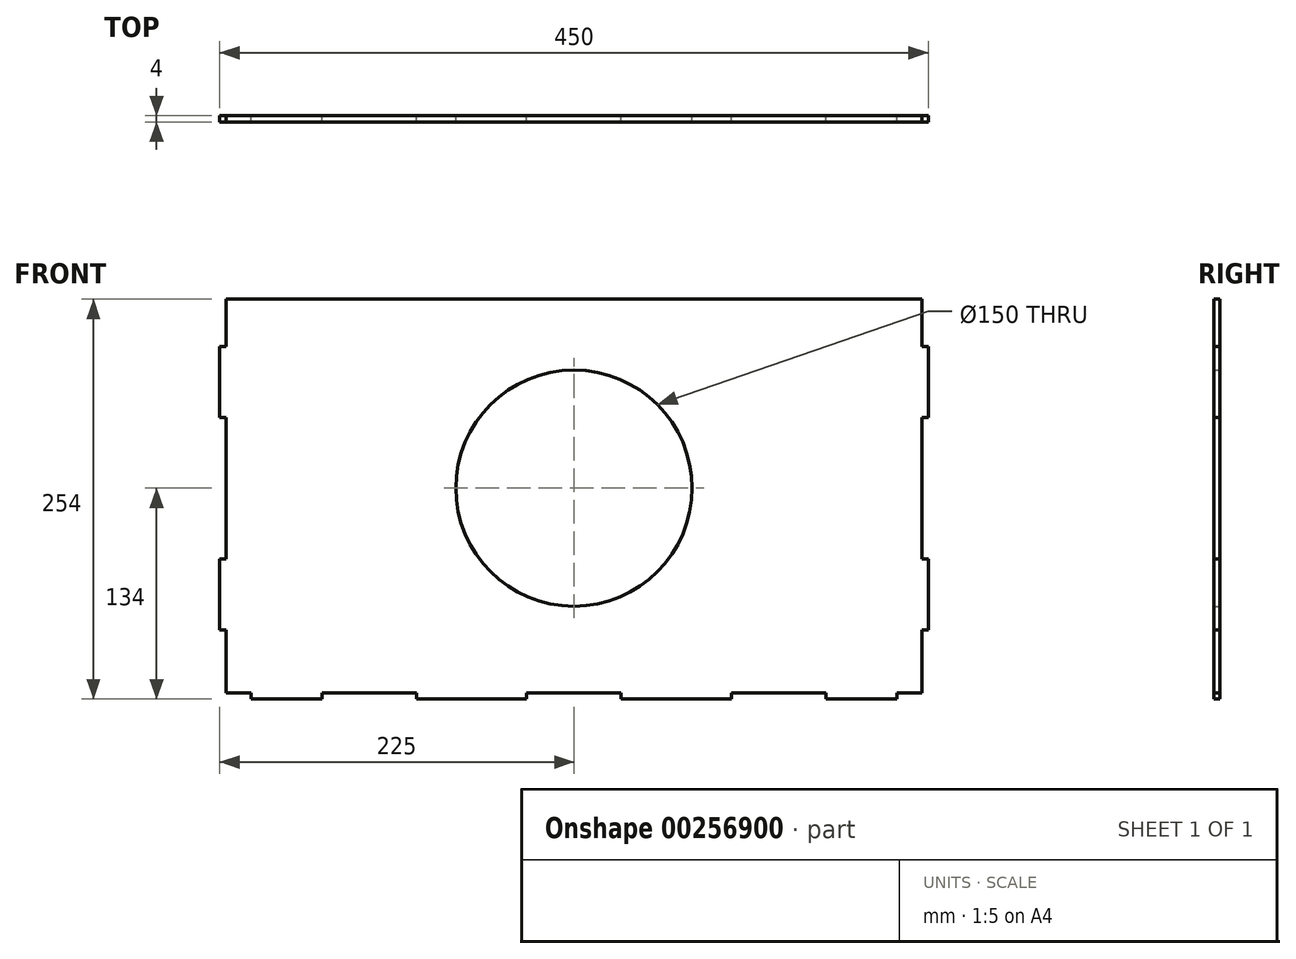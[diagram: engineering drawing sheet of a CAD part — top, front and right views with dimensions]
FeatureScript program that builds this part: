
annotation { "Feature Type Name" : "Feature", "Feature Type Description" : "" }
export const myFeature = defineFeature(function(context is Context, id is Id, definition is map)
    precondition{}
    {
        {
            var Q0;
            Q0=qCreatedBy(makeId("Front.planeOp"),FACE);
            var sketch = newSketch(context, id + "F0", { "sketchPlane" : qUnion([Q0])});
            skLineSegment(sketch, "E0.bottom", {"start": v(-4, 0) * mm, "end": v(-20, 0) * mm});
            skLineSegment(sketch, "E0.top", {"start": v(-4, 250) * mm, "end": v(-446, 250) * mm});
            skLineSegment(sketch, "E0.left", {"start": v(0, 40) * mm, "end": v(0, 85) * mm});
            skLineSegment(sketch, "E1.left", {"start": v(-20, 0) * mm, "end": v(-20, 0) * mm});
            skLineSegment(sketch, "E2", {"start": v(-65, 0) * mm, "end": v(-125, 0) * mm});
            skLineSegment(sketch, "E3", {"start": v(-325, 0) * mm, "end": v(-385, 0) * mm});
            skLineSegment(sketch, "E4", {"start": v(-430, 0) * mm, "end": v(-446, 0) * mm});
            skLineSegment(sketch, "E5", {"start": v(-195, 0) * mm, "end": v(-255, 0) * mm});
            skLineSegment(sketch, "E6", {"start": v(-20, 0) * mm, "end": v(-20, -4) * mm});
            skLineSegment(sketch, "E7", {"start": v(-20, -4) * mm, "end": v(-65, -4) * mm});
            skLineSegment(sketch, "E8", {"start": v(-65, -4) * mm, "end": v(-65, 0) * mm});
            skLineSegment(sketch, "E9", {"start": v(-125, 0) * mm, "end": v(-125, -4) * mm});
            skLineSegment(sketch, "E10", {"start": v(-125, -4) * mm, "end": v(-195, -4) * mm});
            skLineSegment(sketch, "E11", {"start": v(-195, -4) * mm, "end": v(-195, 0) * mm});
            skLineSegment(sketch, "E12", {"start": v(-255, 0) * mm, "end": v(-255, -4) * mm});
            skLineSegment(sketch, "E13", {"start": v(-255, -4) * mm, "end": v(-325, -4) * mm});
            skLineSegment(sketch, "E14", {"start": v(-325, -4) * mm, "end": v(-325, 0) * mm});
            skLineSegment(sketch, "E15", {"start": v(-385, -4) * mm, "end": v(-430, -4) * mm});
            skLineSegment(sketch, "E16", {"start": v(-430, -4) * mm, "end": v(-430, 0) * mm});
            skLineSegment(sketch, "E17", {"start": v(-385, -4) * mm, "end": v(-385, 0) * mm});
            skLineSegment(sketch, "E18.top", {"start": v(-450, 220) * mm, "end": v(-446, 220) * mm});
            skLineSegment(sketch, "E18.right", {"start": v(-446, 250) * mm, "end": v(-446, 220) * mm});
            skLineSegment(sketch, "E19.bottom", {"start": v(-450, 175) * mm, "end": v(-446, 175) * mm});
            skLineSegment(sketch, "E19.top", {"start": v(-450, 85) * mm, "end": v(-446, 85) * mm});
            skLineSegment(sketch, "E19.right", {"start": v(-446, 175) * mm, "end": v(-446, 85) * mm});
            skLineSegment(sketch, "E20.bottom", {"start": v(-450, 40) * mm, "end": v(-446, 40) * mm});
            skLineSegment(sketch, "E20.right", {"start": v(-446, 40) * mm, "end": v(-446, 0) * mm});
            skLineSegment(sketch, "E21", {"start": v(-450, 40) * mm, "end": v(-450, 85) * mm});
            skLineSegment(sketch, "E22", {"start": v(-450, 175) * mm, "end": v(-450, 220) * mm});
            skLineSegment(sketch, "E23", {"start": v(-4, 0) * mm, "end": v(-4, 40) * mm});
            skLineSegment(sketch, "E24", {"start": v(-4, 40) * mm, "end": v(0, 40) * mm});
            skLineSegment(sketch, "E25", {"start": v(0, 85) * mm, "end": v(-4, 85) * mm});
            skLineSegment(sketch, "E26", {"start": v(-4, 85) * mm, "end": v(-4, 175) * mm});
            skLineSegment(sketch, "E27", {"start": v(-4, 175) * mm, "end": v(0, 175) * mm});
            skLineSegment(sketch, "E28", {"start": v(0, 220) * mm, "end": v(-4, 220) * mm});
            skLineSegment(sketch, "E29", {"start": v(0, 175) * mm, "end": v(0, 220) * mm});
            skLineSegment(sketch, "E30", {"start": v(-4, 220) * mm, "end": v(-4, 250) * mm});
            skSolve(sketch);
        }
        {
            var Q0;
            Q0=makeQuery(id+"F0.imprint","IMPRINT",FACE,{"disambiguationData":[TD([[makeQuery(id+"F0.imprint","IMPRINT",EDGE,{"derivedFrom":sQuery(id+"F0.wireOp",EDGE,"E0.bottom")}),-1.0]])]});
            extrude(context, id + "F1", {"entities" : qUnion([Q0]), "depth" : 4 * mm});
        }
        {
            var Q0;
            Q0=makeQuery(id+"F1.opExtrude","CAP_FACE",FACE,{"disambiguationData":[OSD([sQuery(id+"F0.wireOp",EDGE,"E0.bottom"),sQuery(id+"F0.wireOp",EDGE,"E0.top"),sQuery(id+"F0.wireOp",EDGE,"E0.left"),sQuery(id+"F0.wireOp",EDGE,"E2"),sQuery(id+"F0.wireOp",EDGE,"E3"),sQuery(id+"F0.wireOp",EDGE,"E4"),sQuery(id+"F0.wireOp",EDGE,"E5"),sQuery(id+"F0.wireOp",EDGE,"E6"),sQuery(id+"F0.wireOp",EDGE,"E7"),sQuery(id+"F0.wireOp",EDGE,"E8"),sQuery(id+"F0.wireOp",EDGE,"E9"),sQuery(id+"F0.wireOp",EDGE,"E10"),sQuery(id+"F0.wireOp",EDGE,"E11"),sQuery(id+"F0.wireOp",EDGE,"E12"),sQuery(id+"F0.wireOp",EDGE,"E13"),sQuery(id+"F0.wireOp",EDGE,"E14"),sQuery(id+"F0.wireOp",EDGE,"E15"),sQuery(id+"F0.wireOp",EDGE,"E16"),sQuery(id+"F0.wireOp",EDGE,"E17"),sQuery(id+"F0.wireOp",EDGE,"E18.top"),sQuery(id+"F0.wireOp",EDGE,"E18.right"),sQuery(id+"F0.wireOp",EDGE,"E19.bottom"),sQuery(id+"F0.wireOp",EDGE,"E19.top"),sQuery(id+"F0.wireOp",EDGE,"E19.right"),sQuery(id+"F0.wireOp",EDGE,"E20.bottom"),sQuery(id+"F0.wireOp",EDGE,"E20.right"),sQuery(id+"F0.wireOp",EDGE,"E21"),sQuery(id+"F0.wireOp",EDGE,"E22"),sQuery(id+"F0.wireOp",EDGE,"E23"),sQuery(id+"F0.wireOp",EDGE,"E24"),sQuery(id+"F0.wireOp",EDGE,"E25"),sQuery(id+"F0.wireOp",EDGE,"E26"),sQuery(id+"F0.wireOp",EDGE,"E27"),sQuery(id+"F0.wireOp",EDGE,"E28"),sQuery(id+"F0.wireOp",EDGE,"E29"),sQuery(id+"F0.wireOp",EDGE,"E30")])],"isStart":true});
            var sketch = newSketch(context, id + "F2", { "sketchPlane" : qUnion([Q0])});
            skCircle(sketch, "E31", {"center": v(225, 130) * mm, "radius": 75 * mm});
            skPoint(sketch, "E31.centerSnap0", {"position": v(4, 130) * mm});
            skPoint(sketch, "E31.centerSnap1", {"position": v(225, 0) * mm});
            skSolve(sketch);
        }
        {
            var Q0;
            Q0=makeQuery(id+"F2.imprint","IMPRINT",FACE,{"disambiguationData":[TD([[makeQuery(id+"F2.imprint","IMPRINT",EDGE,{"derivedFrom":sQuery(id+"F2.wireOp",EDGE,"E31")}),1.0]])]});
            extrude(context, id + "F3", {"entities" : qUnion([Q0]), "operationType" : NewBodyOperationType.REMOVE, "oppositeDirection" : true, "depth" : 25 * mm});
        }
    });
